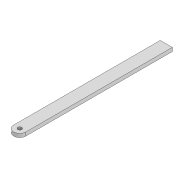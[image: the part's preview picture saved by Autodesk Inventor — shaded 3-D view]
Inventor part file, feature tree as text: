
AUTODESK INVENTOR PART (.ipt)
format: ipt  version: 2022 (Build 260153000, 153)  size: 96,256 bytes
history: native  units: mm
features: extrude x2, sketch x2
ambient origin geometry x8: Origin, YZ Plane, XZ Plane, XY Plane, X Axis, Y Axis, Z Axis, Center Point
bodies: Solid1 (feature_tree)
feature tree (4):
  extrude  "Extrusion1"  Depth=3.3mm
  extrude  "Extrusion2"  Depth=3.0mm
  sketch  "Sketch1"  dims[d0=3.3mm d1=3.3mm]
  sketch  "Sketch3"  dims[d2=10.0mm d3=261.6mm d4=3.3mm d5=153.559mm d6=3.0mm d7=0.0mm d8=100.0mm d9=0.0mm]
